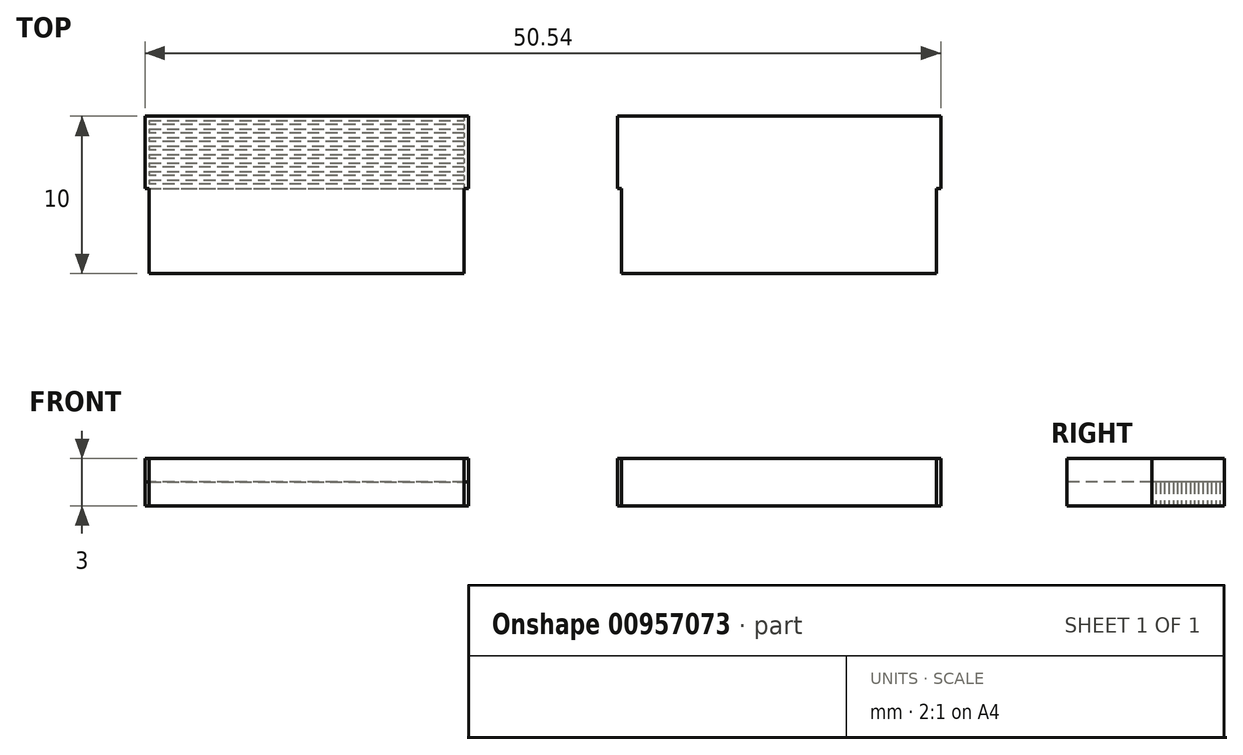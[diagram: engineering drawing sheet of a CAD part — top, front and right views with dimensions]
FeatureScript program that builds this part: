
annotation { "Feature Type Name" : "Feature", "Feature Type Description" : "" }
export const myFeature = defineFeature(function(context is Context, id is Id, definition is map)
    precondition{}
    {
        {
            var Q0;
            Q0=qCreatedBy(makeId("Top.planeOp"),FACE);
            var sketch = newSketch(context, id + "F0", { "sketchPlane" : qUnion([Q0])});
            skLineSegment(sketch, "E0.bottom", {"start": v(10, 5) * mm, "end": v(-10, 5) * mm});
            skLineSegment(sketch, "E0.top", {"start": v(10, -5) * mm, "end": v(-10, -5) * mm});
            skLineSegment(sketch, "E0.left", {"start": v(10, 5) * mm, "end": v(10, -5) * mm});
            skLineSegment(sketch, "E0.right", {"start": v(-10, 5) * mm, "end": v(-10, -5) * mm});
            skPoint(sketch, "E0.middle", {"position": v(0, 0) * mm});
            skLineSegment(sketch, "E1", {"start": v(-10, 4.73) * mm, "end": v(10, 4.73) * mm});
            skLineSegment(sketch, "E2.bottom", {"start": v(-10, 5) * mm, "end": v(-10.27, 5) * mm});
            skLineSegment(sketch, "E2.top", {"start": v(-10, -5) * mm, "end": v(-10.27, -5) * mm});
            skLineSegment(sketch, "E2.right", {"start": v(-10.27, 5) * mm, "end": v(-10.27, -5) * mm});
            skLineSegment(sketch, "E3.MirrorCS", {"start": v(10, 4.46) * mm, "end": v(-10, 4.46) * mm});
            skLineSegment(sketch, "E4.MirrorCS", {"start": v(10, 3.92) * mm, "end": v(-10, 3.92) * mm});
            skLineSegment(sketch, "E5.MirrorCS", {"start": v(-10, 4.19) * mm, "end": v(10, 4.2) * mm});
            skLineSegment(sketch, "E6.MirrorCS", {"start": v(-10, 3.65) * mm, "end": v(10, 3.65) * mm});
            skLineSegment(sketch, "E7.MirrorCS", {"start": v(10, 3.38) * mm, "end": v(-10, 3.38) * mm});
            skLineSegment(sketch, "E8.MirrorCS", {"start": v(-10, 3.11) * mm, "end": v(10, 3.11) * mm});
            skLineSegment(sketch, "E9.MirrorCS", {"start": v(10, 2.84) * mm, "end": v(-10, 2.84) * mm});
            skLineSegment(sketch, "E10.MirrorCS", {"start": v(-10, 2.57) * mm, "end": v(10, 2.57) * mm});
            skLineSegment(sketch, "E11.MirrorCS", {"start": v(10, 2.3) * mm, "end": v(-10, 2.3) * mm});
            skLineSegment(sketch, "E12.MirrorCS", {"start": v(-10, 2.03) * mm, "end": v(10, 2.03) * mm});
            skLineSegment(sketch, "E13.MirrorCS", {"start": v(10, 1.76) * mm, "end": v(-10, 1.76) * mm});
            skLineSegment(sketch, "E14.MirrorCS", {"start": v(-10, 1.49) * mm, "end": v(10, 1.5) * mm});
            skLineSegment(sketch, "E15.MirrorCS", {"start": v(10, 1.22) * mm, "end": v(-10, 1.22) * mm});
            skLineSegment(sketch, "E16.MirrorCS", {"start": v(-10, 0.95) * mm, "end": v(10, 0.95) * mm});
            skLineSegment(sketch, "E17.MirrorCS", {"start": v(10, 0.68) * mm, "end": v(-10, 0.68) * mm});
            skLineSegment(sketch, "E18.MirrorCS", {"start": v(-10, 0.4) * mm, "end": v(10, 0.4) * mm});
            skLineSegment(sketch, "E19.MirrorCS", {"start": v(-10, -5) * mm, "end": v(10, -5) * mm});
            skLineSegment(sketch, "E20.bottom", {"start": v(10, 5) * mm, "end": v(10.27, 5) * mm});
            skLineSegment(sketch, "E20.top", {"start": v(10, -5) * mm, "end": v(10.27, -5) * mm});
            skLineSegment(sketch, "E20.right", {"start": v(10.27, 5) * mm, "end": v(10.27, -5) * mm});
            skLineSegment(sketch, "E21", {"start": v(-10.27, 0.4) * mm, "end": v(10.27, 0.4) * mm});
            skSolve(sketch);
        }
        {
            var Q0;
            {var subQ16=sQuery(id+"F0.wireOp",EDGE,"E2.bottom");Q0=makeQuery(id+"F0.imprint","IMPRINT",FACE,{"disambiguationData":[TD([[makeQuery(id+"F0.imprint","IMPRINT",EDGE,{"derivedFrom":subQ16}),1.0]])]});}
            extrude(context, id + "F1", {"entities" : qUnion([Q0]), "depth" : 3 * mm, "offsetDistance" : 25 * mm});
        }
        {
            var Q0;
            {var subQ0=sQuery(id+"F0.wireOp",EDGE,"E0.bottom");Q0=makeQuery(id+"F0.imprint","IMPRINT",FACE,{"disambiguationData":[TD([[makeQuery(id+"F0.imprint","IMPRINT",EDGE,{"derivedFrom":subQ0}),1.0]])]});}
            var Q1;
            {var subQ0=sQuery(id+"F0.wireOp",EDGE,"E1");Q1=makeQuery(id+"F0.imprint","IMPRINT",FACE,{"disambiguationData":[TD([[makeQuery(id+"F0.imprint","IMPRINT",EDGE,{"derivedFrom":subQ0}),-1.0]])]});}
            var Q2;
            {var subQ0=sQuery(id+"F0.wireOp",EDGE,"E3.MirrorCS");Q2=makeQuery(id+"F0.imprint","IMPRINT",FACE,{"disambiguationData":[TD([[makeQuery(id+"F0.imprint","IMPRINT",EDGE,{"derivedFrom":subQ0}),1.0]])]});}
            var Q3;
            {var subQ0=sQuery(id+"F0.wireOp",EDGE,"E4.MirrorCS");Q3=makeQuery(id+"F0.imprint","IMPRINT",FACE,{"disambiguationData":[TD([[makeQuery(id+"F0.imprint","IMPRINT",EDGE,{"derivedFrom":subQ0}),1.0]])]});}
            var Q4;
            {var subQ0=sQuery(id+"F0.wireOp",EDGE,"E6.MirrorCS");Q4=makeQuery(id+"F0.imprint","IMPRINT",FACE,{"disambiguationData":[TD([[makeQuery(id+"F0.imprint","IMPRINT",EDGE,{"derivedFrom":subQ0}),-1.0]])]});}
            var Q5;
            {var subQ0=sQuery(id+"F0.wireOp",EDGE,"E7.MirrorCS");Q5=makeQuery(id+"F0.imprint","IMPRINT",FACE,{"disambiguationData":[TD([[makeQuery(id+"F0.imprint","IMPRINT",EDGE,{"derivedFrom":subQ0}),1.0]])]});}
            var Q6;
            {var subQ0=sQuery(id+"F0.wireOp",EDGE,"E9.MirrorCS");Q6=makeQuery(id+"F0.imprint","IMPRINT",FACE,{"disambiguationData":[TD([[makeQuery(id+"F0.imprint","IMPRINT",EDGE,{"derivedFrom":subQ0}),1.0]])]});}
            var Q7;
            {var subQ0=sQuery(id+"F0.wireOp",EDGE,"E10.MirrorCS");Q7=makeQuery(id+"F0.imprint","IMPRINT",FACE,{"disambiguationData":[TD([[makeQuery(id+"F0.imprint","IMPRINT",EDGE,{"derivedFrom":subQ0}),-1.0]])]});}
            var Q8;
            {var subQ0=sQuery(id+"F0.wireOp",EDGE,"E11.MirrorCS");Q8=makeQuery(id+"F0.imprint","IMPRINT",FACE,{"disambiguationData":[TD([[makeQuery(id+"F0.imprint","IMPRINT",EDGE,{"derivedFrom":subQ0}),1.0]])]});}
            var Q9;
            {var subQ0=sQuery(id+"F0.wireOp",EDGE,"E13.MirrorCS");Q9=makeQuery(id+"F0.imprint","IMPRINT",FACE,{"disambiguationData":[TD([[makeQuery(id+"F0.imprint","IMPRINT",EDGE,{"derivedFrom":subQ0}),1.0]])]});}
            var Q10;
            {var subQ0=sQuery(id+"F0.wireOp",EDGE,"E14.MirrorCS");Q10=makeQuery(id+"F0.imprint","IMPRINT",FACE,{"disambiguationData":[TD([[makeQuery(id+"F0.imprint","IMPRINT",EDGE,{"derivedFrom":subQ0}),-1.0]])]});}
            var Q11;
            {var subQ0=sQuery(id+"F0.wireOp",EDGE,"E15.MirrorCS");Q11=makeQuery(id+"F0.imprint","IMPRINT",FACE,{"disambiguationData":[TD([[makeQuery(id+"F0.imprint","IMPRINT",EDGE,{"derivedFrom":subQ0}),1.0]])]});}
            var Q12;
            {var subQ0=sQuery(id+"F0.wireOp",EDGE,"E17.MirrorCS");Q12=makeQuery(id+"F0.imprint","IMPRINT",FACE,{"disambiguationData":[TD([[makeQuery(id+"F0.imprint","IMPRINT",EDGE,{"derivedFrom":subQ0}),1.0]])]});}
            var Q13;
            {var subQ0=sQuery(id+"F0.wireOp",EDGE,"E18.MirrorCS");Q13=makeQuery(id+"F0.imprint","IMPRINT",FACE,{"disambiguationData":[TD([[makeQuery(id+"F0.imprint","IMPRINT",EDGE,{"derivedFrom":subQ0}),-1.0]])]});}
            var Q14;
            {var subQ0=sQuery(id+"F0.wireOp",EDGE,"87dff4cc-d492-4903-aaa4-9ca2639ab5790.MirrorCS");Q14=makeQuery(id+"F0.imprint","IMPRINT",FACE,{"disambiguationData":[TD([[makeQuery(id+"F0.imprint","IMPRINT",EDGE,{"derivedFrom":subQ0}),1.0]])]});}
            var Q15;
            {var subQ0=sQuery(id+"F0.wireOp",EDGE,"41ab3706-51a5-4f3e-9648-7aacb442f9cc0.MirrorCS");Q15=makeQuery(id+"F0.imprint","IMPRINT",FACE,{"disambiguationData":[TD([[makeQuery(id+"F0.imprint","IMPRINT",EDGE,{"derivedFrom":subQ0}),1.0]])]});}
            var Q16;
            {var subQ0=sQuery(id+"F0.wireOp",EDGE,"ffffa823-972f-40a5-acad-470e4ebd0f780.MirrorCS");Q16=makeQuery(id+"F0.imprint","IMPRINT",FACE,{"disambiguationData":[TD([[makeQuery(id+"F0.imprint","IMPRINT",EDGE,{"derivedFrom":subQ0}),-1.0]])]});}
            var Q17;
            {var subQ0=sQuery(id+"F0.wireOp",EDGE,"18d8f631-66ae-407d-a703-fdeea4724f1a0.MirrorCS");Q17=makeQuery(id+"F0.imprint","IMPRINT",FACE,{"disambiguationData":[TD([[makeQuery(id+"F0.imprint","IMPRINT",EDGE,{"derivedFrom":subQ0}),1.0]])]});}
            var Q18;
            {var subQ0=sQuery(id+"F0.wireOp",EDGE,"57fad1bf-0eaa-4d78-9149-8f8587bace9e0.MirrorCS");Q18=makeQuery(id+"F0.imprint","IMPRINT",FACE,{"disambiguationData":[TD([[makeQuery(id+"F0.imprint","IMPRINT",EDGE,{"derivedFrom":subQ0}),1.0]])]});}
            var Q19;
            {var subQ0=sQuery(id+"F0.wireOp",EDGE,"3495d730-4adf-43f3-8679-ef0c60d7d5000.MirrorCS");Q19=makeQuery(id+"F0.imprint","IMPRINT",FACE,{"disambiguationData":[TD([[makeQuery(id+"F0.imprint","IMPRINT",EDGE,{"derivedFrom":subQ0}),-1.0]])]});}
            var Q20;
            {var subQ0=sQuery(id+"F0.wireOp",EDGE,"fad44e28-9824-460f-8a45-9381657c69690.MirrorCS");Q20=makeQuery(id+"F0.imprint","IMPRINT",FACE,{"disambiguationData":[TD([[makeQuery(id+"F0.imprint","IMPRINT",EDGE,{"derivedFrom":subQ0}),1.0]])]});}
            var Q21;
            {var subQ0=sQuery(id+"F0.wireOp",EDGE,"23142565-dd91-4a0d-812f-64c14ee8d6a50.MirrorCS");Q21=makeQuery(id+"F0.imprint","IMPRINT",FACE,{"disambiguationData":[TD([[makeQuery(id+"F0.imprint","IMPRINT",EDGE,{"derivedFrom":subQ0}),1.0]])]});}
            var Q22;
            {var subQ0=sQuery(id+"F0.wireOp",EDGE,"826b25fd-4bb7-4322-872f-6a14628de86c0.MirrorCS");Q22=makeQuery(id+"F0.imprint","IMPRINT",FACE,{"disambiguationData":[TD([[makeQuery(id+"F0.imprint","IMPRINT",EDGE,{"derivedFrom":subQ0}),-1.0]])]});}
            var Q23;
            {var subQ0=sQuery(id+"F0.wireOp",EDGE,"58efc46b-88a9-42b5-8359-b4d9ba7942b30.MirrorCS");Q23=makeQuery(id+"F0.imprint","IMPRINT",FACE,{"disambiguationData":[TD([[makeQuery(id+"F0.imprint","IMPRINT",EDGE,{"derivedFrom":subQ0}),1.0]])]});}
            var Q24;
            {var subQ0=sQuery(id+"F0.wireOp",EDGE,"f5abfce5-d8a8-4348-b659-4199fa35e9450.MirrorCS");Q24=makeQuery(id+"F0.imprint","IMPRINT",FACE,{"disambiguationData":[TD([[makeQuery(id+"F0.imprint","IMPRINT",EDGE,{"derivedFrom":subQ0}),1.0]])]});}
            var Q25;
            {var subQ0=sQuery(id+"F0.wireOp",EDGE,"f5e67384-46be-41d7-8ed5-adf4a96e14480.MirrorCS");Q25=makeQuery(id+"F0.imprint","IMPRINT",FACE,{"disambiguationData":[TD([[makeQuery(id+"F0.imprint","IMPRINT",EDGE,{"derivedFrom":subQ0}),-1.0]])]});}
            var Q26;
            {var subQ0=sQuery(id+"F0.wireOp",EDGE,"b3b02505-8e74-4fa5-a726-bd261c9a81610.MirrorCS");Q26=makeQuery(id+"F0.imprint","IMPRINT",FACE,{"disambiguationData":[TD([[makeQuery(id+"F0.imprint","IMPRINT",EDGE,{"derivedFrom":subQ0}),1.0]])]});}
            var Q27;
            {var subQ0=sQuery(id+"F0.wireOp",EDGE,"bb8cc203-0ea3-4b07-8276-ea5ac154ae9f0.MirrorCS");Q27=makeQuery(id+"F0.imprint","IMPRINT",FACE,{"disambiguationData":[TD([[makeQuery(id+"F0.imprint","IMPRINT",EDGE,{"derivedFrom":subQ0}),1.0]])]});}
            extrude(context, id + "F2", {"entities" : qUnion([Q0, Q1, Q2, Q3, Q4, Q5, Q6, Q7, Q8, Q9, Q10, Q11, Q12, Q13, Q14, Q15, Q16, Q17, Q18, Q19, Q20, Q21, Q22, Q23, Q24, Q25, Q26, Q27]), "operationType" : NewBodyOperationType.ADD, "depth" : 3 * mm, "offsetDistance" : 25 * mm});
        }
        {
            var Q0;
            {var subQ16=sQuery(id+"F0.wireOp",EDGE,"E20.bottom");Q0=makeQuery(id+"F0.imprint","IMPRINT",FACE,{"disambiguationData":[TD([[makeQuery(id+"F0.imprint","IMPRINT",EDGE,{"derivedFrom":subQ16}),-1.0]])]});}
            extrude(context, id + "F3", {"entities" : qUnion([Q0]), "depth" : 3 * mm, "offsetDistance" : 25 * mm});
        }
        {
            var Q0;
            {var subQ0=sQuery(id+"F0.wireOp",EDGE,"E4.MirrorCS");Q0=makeQuery(id+"F0.imprint","IMPRINT",FACE,{"disambiguationData":[TD([[makeQuery(id+"F0.imprint","IMPRINT",EDGE,{"derivedFrom":subQ0}),-1.0]])]});}
            var Q1;
            {var subQ0=sQuery(id+"F0.wireOp",EDGE,"E8.MirrorCS");Q1=makeQuery(id+"F0.imprint","IMPRINT",FACE,{"disambiguationData":[TD([[makeQuery(id+"F0.imprint","IMPRINT",EDGE,{"derivedFrom":subQ0}),-1.0]])]});}
            var Q2;
            {var subQ0=sQuery(id+"F0.wireOp",EDGE,"E12.MirrorCS");Q2=makeQuery(id+"F0.imprint","IMPRINT",FACE,{"disambiguationData":[TD([[makeQuery(id+"F0.imprint","IMPRINT",EDGE,{"derivedFrom":subQ0}),-1.0]])]});}
            var Q3;
            {var subQ0=sQuery(id+"F0.wireOp",EDGE,"E16.MirrorCS");Q3=makeQuery(id+"F0.imprint","IMPRINT",FACE,{"disambiguationData":[TD([[makeQuery(id+"F0.imprint","IMPRINT",EDGE,{"derivedFrom":subQ0}),-1.0]])]});}
            var Q4;
            {var subQ0=sQuery(id+"F0.wireOp",EDGE,"15a67bd3-2361-44db-b2c8-4e6e5a9b74e60.MirrorCS");Q4=makeQuery(id+"F0.imprint","IMPRINT",FACE,{"disambiguationData":[TD([[makeQuery(id+"F0.imprint","IMPRINT",EDGE,{"derivedFrom":subQ0}),-1.0]])]});}
            var Q5;
            {var subQ0=sQuery(id+"F0.wireOp",EDGE,"428fac9d-075a-46a2-bddd-a2dfe55257b00.MirrorCS");Q5=makeQuery(id+"F0.imprint","IMPRINT",FACE,{"disambiguationData":[TD([[makeQuery(id+"F0.imprint","IMPRINT",EDGE,{"derivedFrom":subQ0}),-1.0]])]});}
            var Q6;
            {var subQ0=sQuery(id+"F0.wireOp",EDGE,"da81f7ea-5191-4201-a7f4-97f65aa733b20.MirrorCS");Q6=makeQuery(id+"F0.imprint","IMPRINT",FACE,{"disambiguationData":[TD([[makeQuery(id+"F0.imprint","IMPRINT",EDGE,{"derivedFrom":subQ0}),-1.0]])]});}
            var Q7;
            {var subQ0=sQuery(id+"F0.wireOp",EDGE,"97454aad-98a2-4723-8cb6-41b7d56e91b00.MirrorCS");Q7=makeQuery(id+"F0.imprint","IMPRINT",FACE,{"disambiguationData":[TD([[makeQuery(id+"F0.imprint","IMPRINT",EDGE,{"derivedFrom":subQ0}),-1.0]])]});}
            var Q8;
            {var subQ0=sQuery(id+"F0.wireOp",EDGE,"0ba512a5-c1cd-497c-a051-bc5d9319235c0.MirrorCS");Q8=makeQuery(id+"F0.imprint","IMPRINT",FACE,{"disambiguationData":[TD([[makeQuery(id+"F0.imprint","IMPRINT",EDGE,{"derivedFrom":subQ0}),-1.0]])]});}
            extrude(context, id + "F4", {"entities" : qUnion([Q0, Q1, Q2, Q3, Q4, Q5, Q6, Q7, Q8]), "operationType" : NewBodyOperationType.ADD, "depth" : 3 * mm, "offsetDistance" : 25 * mm});
        }
        {
            var Q0;
            {var subQ0=sQuery(id+"F0.wireOp",EDGE,"E0.top");Q0=makeQuery(id+"F0.imprint","IMPRINT",FACE,{"disambiguationData":[TD([[makeQuery(id+"F0.imprint","IMPRINT",EDGE,{"derivedFrom":subQ0}),-1.0]])]});}
            var Q1;
            {var subQ0=sQuery(id+"F0.wireOp",EDGE,"E0.bottom");Q1=makeQuery(id+"F0.imprint","IMPRINT",FACE,{"disambiguationData":[TD([[makeQuery(id+"F0.imprint","IMPRINT",EDGE,{"derivedFrom":subQ0}),1.0]])]});}
            var Q2;
            {var subQ0=sQuery(id+"F0.wireOp",EDGE,"bb8cc203-0ea3-4b07-8276-ea5ac154ae9f0.MirrorCS");Q2=makeQuery(id+"F0.imprint","IMPRINT",FACE,{"disambiguationData":[TD([[makeQuery(id+"F0.imprint","IMPRINT",EDGE,{"derivedFrom":subQ0}),1.0]])]});}
            var Q3;
            {var subQ16=sQuery(id+"F0.wireOp",EDGE,"E20.bottom");Q3=makeQuery(id+"F0.imprint","IMPRINT",FACE,{"disambiguationData":[TD([[makeQuery(id+"F0.imprint","IMPRINT",EDGE,{"derivedFrom":subQ16}),-1.0]])]});}
            var Q4;
            {var subQ16=sQuery(id+"F0.wireOp",EDGE,"E2.bottom");Q4=makeQuery(id+"F0.imprint","IMPRINT",FACE,{"disambiguationData":[TD([[makeQuery(id+"F0.imprint","IMPRINT",EDGE,{"derivedFrom":subQ16}),1.0]])]});}
            var Q5;
            {var subQ0=sQuery(id+"F0.wireOp",EDGE,"E1");Q5=makeQuery(id+"F0.imprint","IMPRINT",FACE,{"disambiguationData":[TD([[makeQuery(id+"F0.imprint","IMPRINT",EDGE,{"derivedFrom":subQ0}),-1.0]])]});}
            var Q6;
            {var subQ0=sQuery(id+"F0.wireOp",EDGE,"3495d730-4adf-43f3-8679-ef0c60d7d5000.MirrorCS");Q6=makeQuery(id+"F0.imprint","IMPRINT",FACE,{"disambiguationData":[TD([[makeQuery(id+"F0.imprint","IMPRINT",EDGE,{"derivedFrom":subQ0}),-1.0]])]});}
            var Q7;
            {var subQ0=sQuery(id+"F0.wireOp",EDGE,"15a67bd3-2361-44db-b2c8-4e6e5a9b74e60.MirrorCS");Q7=makeQuery(id+"F0.imprint","IMPRINT",FACE,{"disambiguationData":[TD([[makeQuery(id+"F0.imprint","IMPRINT",EDGE,{"derivedFrom":subQ0}),-1.0]])]});}
            var Q8;
            {var subQ0=sQuery(id+"F0.wireOp",EDGE,"58efc46b-88a9-42b5-8359-b4d9ba7942b30.MirrorCS");Q8=makeQuery(id+"F0.imprint","IMPRINT",FACE,{"disambiguationData":[TD([[makeQuery(id+"F0.imprint","IMPRINT",EDGE,{"derivedFrom":subQ0}),1.0]])]});}
            var Q9;
            {var subQ0=sQuery(id+"F0.wireOp",EDGE,"E14.MirrorCS");Q9=makeQuery(id+"F0.imprint","IMPRINT",FACE,{"disambiguationData":[TD([[makeQuery(id+"F0.imprint","IMPRINT",EDGE,{"derivedFrom":subQ0}),-1.0]])]});}
            var Q10;
            {var subQ0=sQuery(id+"F0.wireOp",EDGE,"E16.MirrorCS");Q10=makeQuery(id+"F0.imprint","IMPRINT",FACE,{"disambiguationData":[TD([[makeQuery(id+"F0.imprint","IMPRINT",EDGE,{"derivedFrom":subQ0}),-1.0]])]});}
            var Q11;
            {var subQ0=sQuery(id+"F0.wireOp",EDGE,"E4.MirrorCS");Q11=makeQuery(id+"F0.imprint","IMPRINT",FACE,{"disambiguationData":[TD([[makeQuery(id+"F0.imprint","IMPRINT",EDGE,{"derivedFrom":subQ0}),-1.0]])]});}
            var Q12;
            {var subQ0=sQuery(id+"F0.wireOp",EDGE,"87dff4cc-d492-4903-aaa4-9ca2639ab5790.MirrorCS");Q12=makeQuery(id+"F0.imprint","IMPRINT",FACE,{"disambiguationData":[TD([[makeQuery(id+"F0.imprint","IMPRINT",EDGE,{"derivedFrom":subQ0}),1.0]])]});}
            var Q13;
            {var subQ0=sQuery(id+"F0.wireOp",EDGE,"E8.MirrorCS");Q13=makeQuery(id+"F0.imprint","IMPRINT",FACE,{"disambiguationData":[TD([[makeQuery(id+"F0.imprint","IMPRINT",EDGE,{"derivedFrom":subQ0}),-1.0]])]});}
            var Q14;
            {var subQ0=sQuery(id+"F0.wireOp",EDGE,"57fad1bf-0eaa-4d78-9149-8f8587bace9e0.MirrorCS");Q14=makeQuery(id+"F0.imprint","IMPRINT",FACE,{"disambiguationData":[TD([[makeQuery(id+"F0.imprint","IMPRINT",EDGE,{"derivedFrom":subQ0}),1.0]])]});}
            var Q15;
            {var subQ0=sQuery(id+"F0.wireOp",EDGE,"E10.MirrorCS");Q15=makeQuery(id+"F0.imprint","IMPRINT",FACE,{"disambiguationData":[TD([[makeQuery(id+"F0.imprint","IMPRINT",EDGE,{"derivedFrom":subQ0}),-1.0]])]});}
            var Q16;
            {var subQ0=sQuery(id+"F0.wireOp",EDGE,"41ab3706-51a5-4f3e-9648-7aacb442f9cc0.MirrorCS");Q16=makeQuery(id+"F0.imprint","IMPRINT",FACE,{"disambiguationData":[TD([[makeQuery(id+"F0.imprint","IMPRINT",EDGE,{"derivedFrom":subQ0}),1.0]])]});}
            var Q17;
            {var subQ0=sQuery(id+"F0.wireOp",EDGE,"da81f7ea-5191-4201-a7f4-97f65aa733b20.MirrorCS");Q17=makeQuery(id+"F0.imprint","IMPRINT",FACE,{"disambiguationData":[TD([[makeQuery(id+"F0.imprint","IMPRINT",EDGE,{"derivedFrom":subQ0}),-1.0]])]});}
            var Q18;
            {var subQ0=sQuery(id+"F0.wireOp",EDGE,"E6.MirrorCS");Q18=makeQuery(id+"F0.imprint","IMPRINT",FACE,{"disambiguationData":[TD([[makeQuery(id+"F0.imprint","IMPRINT",EDGE,{"derivedFrom":subQ0}),-1.0]])]});}
            var Q19;
            {var subQ0=sQuery(id+"F0.wireOp",EDGE,"0ba512a5-c1cd-497c-a051-bc5d9319235c0.MirrorCS");Q19=makeQuery(id+"F0.imprint","IMPRINT",FACE,{"disambiguationData":[TD([[makeQuery(id+"F0.imprint","IMPRINT",EDGE,{"derivedFrom":subQ0}),-1.0]])]});}
            var Q20;
            {var subQ0=sQuery(id+"F0.wireOp",EDGE,"23142565-dd91-4a0d-812f-64c14ee8d6a50.MirrorCS");Q20=makeQuery(id+"F0.imprint","IMPRINT",FACE,{"disambiguationData":[TD([[makeQuery(id+"F0.imprint","IMPRINT",EDGE,{"derivedFrom":subQ0}),1.0]])]});}
            var Q21;
            {var subQ0=sQuery(id+"F0.wireOp",EDGE,"E4.MirrorCS");Q21=makeQuery(id+"F0.imprint","IMPRINT",FACE,{"disambiguationData":[TD([[makeQuery(id+"F0.imprint","IMPRINT",EDGE,{"derivedFrom":subQ0}),1.0]])]});}
            var Q22;
            {var subQ0=sQuery(id+"F0.wireOp",EDGE,"E13.MirrorCS");Q22=makeQuery(id+"F0.imprint","IMPRINT",FACE,{"disambiguationData":[TD([[makeQuery(id+"F0.imprint","IMPRINT",EDGE,{"derivedFrom":subQ0}),1.0]])]});}
            var Q23;
            {var subQ0=sQuery(id+"F0.wireOp",EDGE,"E11.MirrorCS");Q23=makeQuery(id+"F0.imprint","IMPRINT",FACE,{"disambiguationData":[TD([[makeQuery(id+"F0.imprint","IMPRINT",EDGE,{"derivedFrom":subQ0}),1.0]])]});}
            var Q24;
            {var subQ0=sQuery(id+"F0.wireOp",EDGE,"E7.MirrorCS");Q24=makeQuery(id+"F0.imprint","IMPRINT",FACE,{"disambiguationData":[TD([[makeQuery(id+"F0.imprint","IMPRINT",EDGE,{"derivedFrom":subQ0}),1.0]])]});}
            var Q25;
            {var subQ0=sQuery(id+"F0.wireOp",EDGE,"E9.MirrorCS");Q25=makeQuery(id+"F0.imprint","IMPRINT",FACE,{"disambiguationData":[TD([[makeQuery(id+"F0.imprint","IMPRINT",EDGE,{"derivedFrom":subQ0}),1.0]])]});}
            var Q26;
            {var subQ0=sQuery(id+"F0.wireOp",EDGE,"fad44e28-9824-460f-8a45-9381657c69690.MirrorCS");Q26=makeQuery(id+"F0.imprint","IMPRINT",FACE,{"disambiguationData":[TD([[makeQuery(id+"F0.imprint","IMPRINT",EDGE,{"derivedFrom":subQ0}),1.0]])]});}
            var Q27;
            {var subQ0=sQuery(id+"F0.wireOp",EDGE,"826b25fd-4bb7-4322-872f-6a14628de86c0.MirrorCS");Q27=makeQuery(id+"F0.imprint","IMPRINT",FACE,{"disambiguationData":[TD([[makeQuery(id+"F0.imprint","IMPRINT",EDGE,{"derivedFrom":subQ0}),-1.0]])]});}
            var Q28;
            {var subQ0=sQuery(id+"F0.wireOp",EDGE,"f5e67384-46be-41d7-8ed5-adf4a96e14480.MirrorCS");Q28=makeQuery(id+"F0.imprint","IMPRINT",FACE,{"disambiguationData":[TD([[makeQuery(id+"F0.imprint","IMPRINT",EDGE,{"derivedFrom":subQ0}),-1.0]])]});}
            var Q29;
            {var subQ0=sQuery(id+"F0.wireOp",EDGE,"f5abfce5-d8a8-4348-b659-4199fa35e9450.MirrorCS");Q29=makeQuery(id+"F0.imprint","IMPRINT",FACE,{"disambiguationData":[TD([[makeQuery(id+"F0.imprint","IMPRINT",EDGE,{"derivedFrom":subQ0}),1.0]])]});}
            var Q30;
            {var subQ0=sQuery(id+"F0.wireOp",EDGE,"E12.MirrorCS");Q30=makeQuery(id+"F0.imprint","IMPRINT",FACE,{"disambiguationData":[TD([[makeQuery(id+"F0.imprint","IMPRINT",EDGE,{"derivedFrom":subQ0}),-1.0]])]});}
            var Q31;
            {var subQ0=sQuery(id+"F0.wireOp",EDGE,"ffffa823-972f-40a5-acad-470e4ebd0f780.MirrorCS");Q31=makeQuery(id+"F0.imprint","IMPRINT",FACE,{"disambiguationData":[TD([[makeQuery(id+"F0.imprint","IMPRINT",EDGE,{"derivedFrom":subQ0}),-1.0]])]});}
            var Q32;
            {var subQ0=sQuery(id+"F0.wireOp",EDGE,"E18.MirrorCS");Q32=makeQuery(id+"F0.imprint","IMPRINT",FACE,{"disambiguationData":[TD([[makeQuery(id+"F0.imprint","IMPRINT",EDGE,{"derivedFrom":subQ0}),-1.0]])]});}
            var Q33;
            {var subQ0=sQuery(id+"F0.wireOp",EDGE,"97454aad-98a2-4723-8cb6-41b7d56e91b00.MirrorCS");Q33=makeQuery(id+"F0.imprint","IMPRINT",FACE,{"disambiguationData":[TD([[makeQuery(id+"F0.imprint","IMPRINT",EDGE,{"derivedFrom":subQ0}),-1.0]])]});}
            var Q34;
            {var subQ0=sQuery(id+"F0.wireOp",EDGE,"E3.MirrorCS");Q34=makeQuery(id+"F0.imprint","IMPRINT",FACE,{"disambiguationData":[TD([[makeQuery(id+"F0.imprint","IMPRINT",EDGE,{"derivedFrom":subQ0}),1.0]])]});}
            var Q35;
            {var subQ0=sQuery(id+"F0.wireOp",EDGE,"b3b02505-8e74-4fa5-a726-bd261c9a81610.MirrorCS");Q35=makeQuery(id+"F0.imprint","IMPRINT",FACE,{"disambiguationData":[TD([[makeQuery(id+"F0.imprint","IMPRINT",EDGE,{"derivedFrom":subQ0}),1.0]])]});}
            var Q36;
            {var subQ0=sQuery(id+"F0.wireOp",EDGE,"18d8f631-66ae-407d-a703-fdeea4724f1a0.MirrorCS");Q36=makeQuery(id+"F0.imprint","IMPRINT",FACE,{"disambiguationData":[TD([[makeQuery(id+"F0.imprint","IMPRINT",EDGE,{"derivedFrom":subQ0}),1.0]])]});}
            var Q37;
            {var subQ0=sQuery(id+"F0.wireOp",EDGE,"428fac9d-075a-46a2-bddd-a2dfe55257b00.MirrorCS");Q37=makeQuery(id+"F0.imprint","IMPRINT",FACE,{"disambiguationData":[TD([[makeQuery(id+"F0.imprint","IMPRINT",EDGE,{"derivedFrom":subQ0}),-1.0]])]});}
            var Q38;
            {var subQ0=sQuery(id+"F0.wireOp",EDGE,"E15.MirrorCS");Q38=makeQuery(id+"F0.imprint","IMPRINT",FACE,{"disambiguationData":[TD([[makeQuery(id+"F0.imprint","IMPRINT",EDGE,{"derivedFrom":subQ0}),1.0]])]});}
            var Q39;
            {var subQ0=sQuery(id+"F0.wireOp",EDGE,"E17.MirrorCS");Q39=makeQuery(id+"F0.imprint","IMPRINT",FACE,{"disambiguationData":[TD([[makeQuery(id+"F0.imprint","IMPRINT",EDGE,{"derivedFrom":subQ0}),1.0]])]});}
            extrude(context, id + "F5", {"entities" : qUnion([Q0, Q1, Q2, Q3, Q4, Q5, Q6, Q7, Q8, Q9, Q10, Q11, Q12, Q13, Q14, Q15, Q16, Q17, Q18, Q19, Q20, Q21, Q22, Q23, Q24, Q25, Q26, Q27, Q28, Q29, Q30, Q31, Q32, Q33, Q34, Q35, Q36, Q37, Q38, Q39]), "depth" : 3 * mm, "offsetDistance" : 25 * mm});
        }
        {
            var Q0;
            {var subQ16=sQuery(id+"F0.wireOp",EDGE,"E2.bottom");Q0=makeQuery(id+"F0.imprint","IMPRINT",FACE,{"disambiguationData":[TD([[makeQuery(id+"F0.imprint","IMPRINT",EDGE,{"derivedFrom":subQ16}),1.0]])]});}
            var Q1;
            {var subQ0=sQuery(id+"F0.wireOp",EDGE,"E0.bottom");Q1=makeQuery(id+"F0.imprint","IMPRINT",FACE,{"disambiguationData":[TD([[makeQuery(id+"F0.imprint","IMPRINT",EDGE,{"derivedFrom":subQ0}),1.0]])]});}
            var Q2;
            {var subQ0=sQuery(id+"F0.wireOp",EDGE,"E3.MirrorCS");Q2=makeQuery(id+"F0.imprint","IMPRINT",FACE,{"disambiguationData":[TD([[makeQuery(id+"F0.imprint","IMPRINT",EDGE,{"derivedFrom":subQ0}),1.0]])]});}
            var Q3;
            {var subQ0=sQuery(id+"F0.wireOp",EDGE,"E4.MirrorCS");Q3=makeQuery(id+"F0.imprint","IMPRINT",FACE,{"disambiguationData":[TD([[makeQuery(id+"F0.imprint","IMPRINT",EDGE,{"derivedFrom":subQ0}),1.0]])]});}
            var Q4;
            {var subQ0=sQuery(id+"F0.wireOp",EDGE,"E7.MirrorCS");Q4=makeQuery(id+"F0.imprint","IMPRINT",FACE,{"disambiguationData":[TD([[makeQuery(id+"F0.imprint","IMPRINT",EDGE,{"derivedFrom":subQ0}),1.0]])]});}
            var Q5;
            {var subQ0=sQuery(id+"F0.wireOp",EDGE,"E9.MirrorCS");Q5=makeQuery(id+"F0.imprint","IMPRINT",FACE,{"disambiguationData":[TD([[makeQuery(id+"F0.imprint","IMPRINT",EDGE,{"derivedFrom":subQ0}),1.0]])]});}
            var Q6;
            {var subQ0=sQuery(id+"F0.wireOp",EDGE,"E11.MirrorCS");Q6=makeQuery(id+"F0.imprint","IMPRINT",FACE,{"disambiguationData":[TD([[makeQuery(id+"F0.imprint","IMPRINT",EDGE,{"derivedFrom":subQ0}),1.0]])]});}
            var Q7;
            {var subQ0=sQuery(id+"F0.wireOp",EDGE,"E13.MirrorCS");Q7=makeQuery(id+"F0.imprint","IMPRINT",FACE,{"disambiguationData":[TD([[makeQuery(id+"F0.imprint","IMPRINT",EDGE,{"derivedFrom":subQ0}),1.0]])]});}
            var Q8;
            {var subQ0=sQuery(id+"F0.wireOp",EDGE,"E15.MirrorCS");Q8=makeQuery(id+"F0.imprint","IMPRINT",FACE,{"disambiguationData":[TD([[makeQuery(id+"F0.imprint","IMPRINT",EDGE,{"derivedFrom":subQ0}),1.0]])]});}
            var Q9;
            {var subQ0=sQuery(id+"F0.wireOp",EDGE,"E17.MirrorCS");Q9=makeQuery(id+"F0.imprint","IMPRINT",FACE,{"disambiguationData":[TD([[makeQuery(id+"F0.imprint","IMPRINT",EDGE,{"derivedFrom":subQ0}),1.0]])]});}
            var Q10;
            {var subQ0=sQuery(id+"F0.wireOp",EDGE,"87dff4cc-d492-4903-aaa4-9ca2639ab5790.MirrorCS");Q10=makeQuery(id+"F0.imprint","IMPRINT",FACE,{"disambiguationData":[TD([[makeQuery(id+"F0.imprint","IMPRINT",EDGE,{"derivedFrom":subQ0}),1.0]])]});}
            var Q11;
            {var subQ0=sQuery(id+"F0.wireOp",EDGE,"41ab3706-51a5-4f3e-9648-7aacb442f9cc0.MirrorCS");Q11=makeQuery(id+"F0.imprint","IMPRINT",FACE,{"disambiguationData":[TD([[makeQuery(id+"F0.imprint","IMPRINT",EDGE,{"derivedFrom":subQ0}),1.0]])]});}
            var Q12;
            {var subQ0=sQuery(id+"F0.wireOp",EDGE,"18d8f631-66ae-407d-a703-fdeea4724f1a0.MirrorCS");Q12=makeQuery(id+"F0.imprint","IMPRINT",FACE,{"disambiguationData":[TD([[makeQuery(id+"F0.imprint","IMPRINT",EDGE,{"derivedFrom":subQ0}),1.0]])]});}
            var Q13;
            {var subQ0=sQuery(id+"F0.wireOp",EDGE,"57fad1bf-0eaa-4d78-9149-8f8587bace9e0.MirrorCS");Q13=makeQuery(id+"F0.imprint","IMPRINT",FACE,{"disambiguationData":[TD([[makeQuery(id+"F0.imprint","IMPRINT",EDGE,{"derivedFrom":subQ0}),1.0]])]});}
            var Q14;
            {var subQ0=sQuery(id+"F0.wireOp",EDGE,"fad44e28-9824-460f-8a45-9381657c69690.MirrorCS");Q14=makeQuery(id+"F0.imprint","IMPRINT",FACE,{"disambiguationData":[TD([[makeQuery(id+"F0.imprint","IMPRINT",EDGE,{"derivedFrom":subQ0}),1.0]])]});}
            var Q15;
            {var subQ0=sQuery(id+"F0.wireOp",EDGE,"23142565-dd91-4a0d-812f-64c14ee8d6a50.MirrorCS");Q15=makeQuery(id+"F0.imprint","IMPRINT",FACE,{"disambiguationData":[TD([[makeQuery(id+"F0.imprint","IMPRINT",EDGE,{"derivedFrom":subQ0}),1.0]])]});}
            var Q16;
            {var subQ0=sQuery(id+"F0.wireOp",EDGE,"58efc46b-88a9-42b5-8359-b4d9ba7942b30.MirrorCS");Q16=makeQuery(id+"F0.imprint","IMPRINT",FACE,{"disambiguationData":[TD([[makeQuery(id+"F0.imprint","IMPRINT",EDGE,{"derivedFrom":subQ0}),1.0]])]});}
            var Q17;
            {var subQ0=sQuery(id+"F0.wireOp",EDGE,"f5abfce5-d8a8-4348-b659-4199fa35e9450.MirrorCS");Q17=makeQuery(id+"F0.imprint","IMPRINT",FACE,{"disambiguationData":[TD([[makeQuery(id+"F0.imprint","IMPRINT",EDGE,{"derivedFrom":subQ0}),1.0]])]});}
            var Q18;
            {var subQ0=sQuery(id+"F0.wireOp",EDGE,"b3b02505-8e74-4fa5-a726-bd261c9a81610.MirrorCS");Q18=makeQuery(id+"F0.imprint","IMPRINT",FACE,{"disambiguationData":[TD([[makeQuery(id+"F0.imprint","IMPRINT",EDGE,{"derivedFrom":subQ0}),1.0]])]});}
            var Q19;
            {var subQ0=sQuery(id+"F0.wireOp",EDGE,"bb8cc203-0ea3-4b07-8276-ea5ac154ae9f0.MirrorCS");Q19=makeQuery(id+"F0.imprint","IMPRINT",FACE,{"disambiguationData":[TD([[makeQuery(id+"F0.imprint","IMPRINT",EDGE,{"derivedFrom":subQ0}),1.0]])]});}
            extrude(context, id + "F6", {"entities" : qUnion([Q0, Q1, Q2, Q3, Q4, Q5, Q6, Q7, Q8, Q9, Q10, Q11, Q12, Q13, Q14, Q15, Q16, Q17, Q18, Q19]), "depth" : 1.5 * mm, "offsetDistance" : 25 * mm});
        }
        {
            var Q0;
            {var subQ16=sQuery(id+"F0.wireOp",EDGE,"E20.bottom");Q0=makeQuery(id+"F0.imprint","IMPRINT",FACE,{"disambiguationData":[TD([[makeQuery(id+"F0.imprint","IMPRINT",EDGE,{"derivedFrom":subQ16}),-1.0]])]});}
            var Q1;
            {var subQ0=sQuery(id+"F0.wireOp",EDGE,"E1");Q1=makeQuery(id+"F0.imprint","IMPRINT",FACE,{"disambiguationData":[TD([[makeQuery(id+"F0.imprint","IMPRINT",EDGE,{"derivedFrom":subQ0}),-1.0]])]});}
            var Q2;
            {var subQ0=sQuery(id+"F0.wireOp",EDGE,"E4.MirrorCS");Q2=makeQuery(id+"F0.imprint","IMPRINT",FACE,{"disambiguationData":[TD([[makeQuery(id+"F0.imprint","IMPRINT",EDGE,{"derivedFrom":subQ0}),-1.0]])]});}
            var Q3;
            {var subQ0=sQuery(id+"F0.wireOp",EDGE,"E6.MirrorCS");Q3=makeQuery(id+"F0.imprint","IMPRINT",FACE,{"disambiguationData":[TD([[makeQuery(id+"F0.imprint","IMPRINT",EDGE,{"derivedFrom":subQ0}),-1.0]])]});}
            var Q4;
            {var subQ0=sQuery(id+"F0.wireOp",EDGE,"E8.MirrorCS");Q4=makeQuery(id+"F0.imprint","IMPRINT",FACE,{"disambiguationData":[TD([[makeQuery(id+"F0.imprint","IMPRINT",EDGE,{"derivedFrom":subQ0}),-1.0]])]});}
            var Q5;
            {var subQ0=sQuery(id+"F0.wireOp",EDGE,"E10.MirrorCS");Q5=makeQuery(id+"F0.imprint","IMPRINT",FACE,{"disambiguationData":[TD([[makeQuery(id+"F0.imprint","IMPRINT",EDGE,{"derivedFrom":subQ0}),-1.0]])]});}
            var Q6;
            {var subQ0=sQuery(id+"F0.wireOp",EDGE,"E12.MirrorCS");Q6=makeQuery(id+"F0.imprint","IMPRINT",FACE,{"disambiguationData":[TD([[makeQuery(id+"F0.imprint","IMPRINT",EDGE,{"derivedFrom":subQ0}),-1.0]])]});}
            var Q7;
            {var subQ0=sQuery(id+"F0.wireOp",EDGE,"E14.MirrorCS");Q7=makeQuery(id+"F0.imprint","IMPRINT",FACE,{"disambiguationData":[TD([[makeQuery(id+"F0.imprint","IMPRINT",EDGE,{"derivedFrom":subQ0}),-1.0]])]});}
            var Q8;
            {var subQ0=sQuery(id+"F0.wireOp",EDGE,"E16.MirrorCS");Q8=makeQuery(id+"F0.imprint","IMPRINT",FACE,{"disambiguationData":[TD([[makeQuery(id+"F0.imprint","IMPRINT",EDGE,{"derivedFrom":subQ0}),-1.0]])]});}
            var Q9;
            {var subQ0=sQuery(id+"F0.wireOp",EDGE,"E18.MirrorCS");Q9=makeQuery(id+"F0.imprint","IMPRINT",FACE,{"disambiguationData":[TD([[makeQuery(id+"F0.imprint","IMPRINT",EDGE,{"derivedFrom":subQ0}),-1.0]])]});}
            var Q10;
            {var subQ0=sQuery(id+"F0.wireOp",EDGE,"15a67bd3-2361-44db-b2c8-4e6e5a9b74e60.MirrorCS");Q10=makeQuery(id+"F0.imprint","IMPRINT",FACE,{"disambiguationData":[TD([[makeQuery(id+"F0.imprint","IMPRINT",EDGE,{"derivedFrom":subQ0}),-1.0]])]});}
            var Q11;
            {var subQ0=sQuery(id+"F0.wireOp",EDGE,"ffffa823-972f-40a5-acad-470e4ebd0f780.MirrorCS");Q11=makeQuery(id+"F0.imprint","IMPRINT",FACE,{"disambiguationData":[TD([[makeQuery(id+"F0.imprint","IMPRINT",EDGE,{"derivedFrom":subQ0}),-1.0]])]});}
            var Q12;
            {var subQ0=sQuery(id+"F0.wireOp",EDGE,"428fac9d-075a-46a2-bddd-a2dfe55257b00.MirrorCS");Q12=makeQuery(id+"F0.imprint","IMPRINT",FACE,{"disambiguationData":[TD([[makeQuery(id+"F0.imprint","IMPRINT",EDGE,{"derivedFrom":subQ0}),-1.0]])]});}
            var Q13;
            {var subQ0=sQuery(id+"F0.wireOp",EDGE,"3495d730-4adf-43f3-8679-ef0c60d7d5000.MirrorCS");Q13=makeQuery(id+"F0.imprint","IMPRINT",FACE,{"disambiguationData":[TD([[makeQuery(id+"F0.imprint","IMPRINT",EDGE,{"derivedFrom":subQ0}),-1.0]])]});}
            var Q14;
            {var subQ0=sQuery(id+"F0.wireOp",EDGE,"da81f7ea-5191-4201-a7f4-97f65aa733b20.MirrorCS");Q14=makeQuery(id+"F0.imprint","IMPRINT",FACE,{"disambiguationData":[TD([[makeQuery(id+"F0.imprint","IMPRINT",EDGE,{"derivedFrom":subQ0}),-1.0]])]});}
            var Q15;
            {var subQ0=sQuery(id+"F0.wireOp",EDGE,"826b25fd-4bb7-4322-872f-6a14628de86c0.MirrorCS");Q15=makeQuery(id+"F0.imprint","IMPRINT",FACE,{"disambiguationData":[TD([[makeQuery(id+"F0.imprint","IMPRINT",EDGE,{"derivedFrom":subQ0}),-1.0]])]});}
            var Q16;
            {var subQ0=sQuery(id+"F0.wireOp",EDGE,"97454aad-98a2-4723-8cb6-41b7d56e91b00.MirrorCS");Q16=makeQuery(id+"F0.imprint","IMPRINT",FACE,{"disambiguationData":[TD([[makeQuery(id+"F0.imprint","IMPRINT",EDGE,{"derivedFrom":subQ0}),-1.0]])]});}
            var Q17;
            {var subQ0=sQuery(id+"F0.wireOp",EDGE,"f5e67384-46be-41d7-8ed5-adf4a96e14480.MirrorCS");Q17=makeQuery(id+"F0.imprint","IMPRINT",FACE,{"disambiguationData":[TD([[makeQuery(id+"F0.imprint","IMPRINT",EDGE,{"derivedFrom":subQ0}),-1.0]])]});}
            var Q18;
            {var subQ0=sQuery(id+"F0.wireOp",EDGE,"0ba512a5-c1cd-497c-a051-bc5d9319235c0.MirrorCS");Q18=makeQuery(id+"F0.imprint","IMPRINT",FACE,{"disambiguationData":[TD([[makeQuery(id+"F0.imprint","IMPRINT",EDGE,{"derivedFrom":subQ0}),-1.0]])]});}
            extrude(context, id + "F7", {"entities" : qUnion([Q0, Q1, Q2, Q3, Q4, Q5, Q6, Q7, Q8, Q9, Q10, Q11, Q12, Q13, Q14, Q15, Q16, Q17, Q18]), "depth" : 1.5 * mm, "offsetDistance" : 25 * mm});
        }
        {
            var Q0;
            Q0=makeQuery(id+"F5.opExtrude","SWEPT_BODY",BODY,{"disambiguationData":[OSD([sQuery(id+"F0.wireOp",EDGE,"E0.bottom"),sQuery(id+"F0.wireOp",EDGE,"E2.bottom"),sQuery(id+"F0.wireOp",EDGE,"E2.right"),sQuery(id+"F0.wireOp",EDGE,"E20.bottom"),sQuery(id+"F0.wireOp",EDGE,"E20.right"),sQuery(id+"F0.wireOp",EDGE,"E21")])]});
            transform(context, id + "F8", {"entities" : qUnion([Q0]), "transformType" : TransformType.TRANSLATION_3D, "dx" : 30 * mm, "dy" : 0 * mm, "dz" : 0 * mm, "makeCopy" : true});
        }
    });
